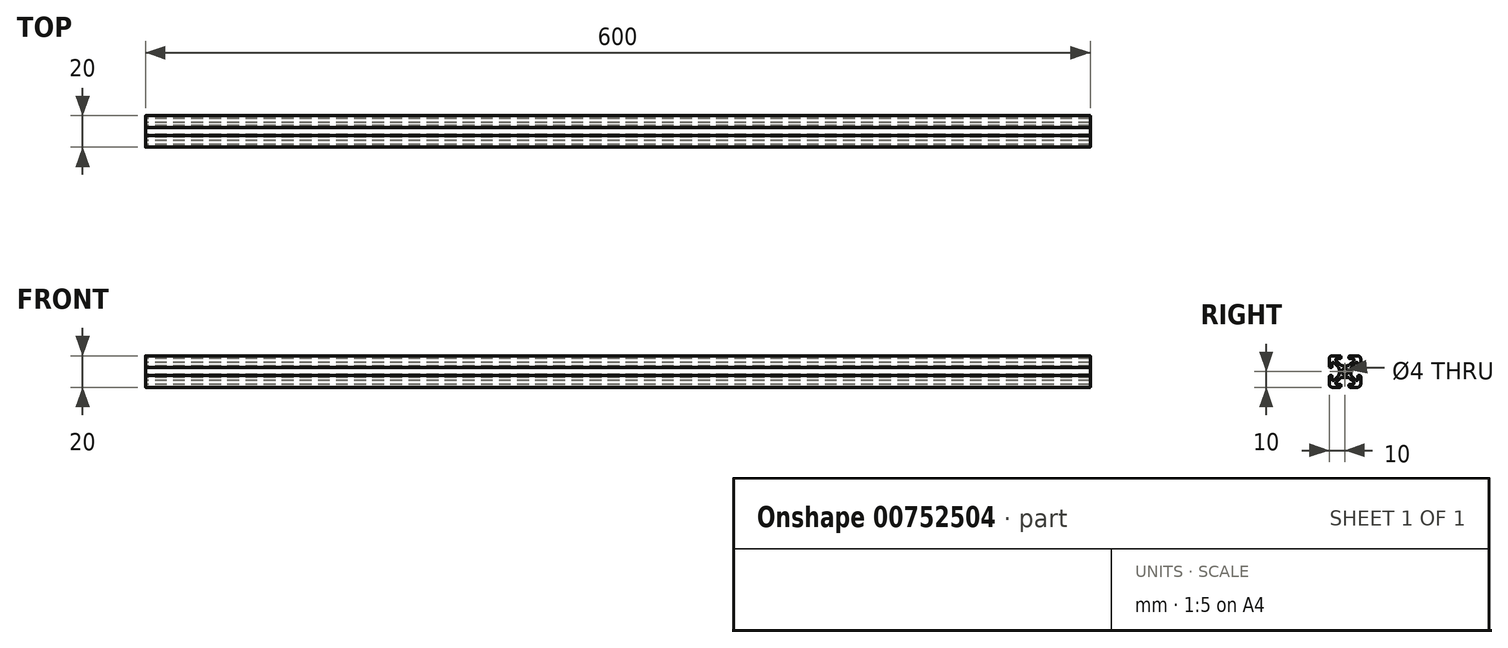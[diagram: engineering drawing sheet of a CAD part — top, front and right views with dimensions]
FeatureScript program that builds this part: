
annotation { "Feature Type Name" : "Feature", "Feature Type Description" : "" }
export const myFeature = defineFeature(function(context is Context, id is Id, definition is map)
    precondition{}
    {
        {
            var Q0;
            Q0=qCreatedBy(makeId("Right.planeOp"),FACE);
            var sketch = newSketch(context, id + "F0", { "sketchPlane" : qUnion([Q0])});
            skLineSegment(sketch, "E0.bottom", {"start": v(-8, 10) * mm, "end": v(-3.3, 10) * mm});
            skLineSegment(sketch, "E0.top", {"start": v(-8, -10) * mm, "end": v(-3.3, -10) * mm});
            skLineSegment(sketch, "E0.right", {"start": v(10, 8) * mm, "end": v(10, 3.3) * mm});
            skLineSegment(sketch, "E1", {"start": v(0, 31.7) * mm, "end": v(0, -24.01) * mm, "construction": true});
            skLineSegment(sketch, "E2", {"start": v(-29.71, 0) * mm, "end": v(21.95, 0) * mm, "construction": true});
            skLineSegment(sketch, "E3", {"start": v(-2.5, 9.2) * mm, "end": v(-2.5, 8.5) * mm});
            skLineSegment(sketch, "E4", {"start": v(-2.8, 8.2) * mm, "end": v(-4.92, 8.2) * mm});
            skLineSegment(sketch, "E5", {"start": v(-5.5, 6.78) * mm, "end": v(-3.25, 4.53) * mm});
            skLineSegment(sketch, "E6", {"start": v(-1.13, 3.65) * mm, "end": v(1.14, 3.65) * mm});
            skLineSegment(sketch, "E7", {"start": v(3.25, 4.53) * mm, "end": v(5.5, 6.78) * mm});
            skLineSegment(sketch, "E8", {"start": v(4.92, 8.2) * mm, "end": v(2.8, 8.2) * mm});
            skLineSegment(sketch, "E9", {"start": v(2.5, 8.5) * mm, "end": v(2.5, 9.2) * mm});
            skLineSegment(sketch, "E10.trimOffspring", {"start": v(3.3, 10) * mm, "end": v(8, 10) * mm});
            skArc(sketch, "E11.filletArc", {"start": v(-8, 10) * mm, "mid": v(-9.41, 9.41) * mm, "end": v(-10, 8) * mm});
            skArc(sketch, "E12.filletArc", {"start": v(-10, -8) * mm, "mid": v(-9.41, -9.41) * mm, "end": v(-8, -10) * mm});
            skArc(sketch, "E13.filletArc", {"start": v(8, -10) * mm, "mid": v(9.41, -9.41) * mm, "end": v(10, -8) * mm});
            skArc(sketch, "E14.filletArc", {"start": v(10, 8) * mm, "mid": v(9.41, 9.41) * mm, "end": v(8, 10) * mm});
            skPoint(sketch, "E15.visualSharp", {"position": v(-9.03, 10.3) * mm});
            skArc(sketch, "E15.filletArc", {"start": v(-4.92, 8.2) * mm, "mid": v(-5.69, 7.69) * mm, "end": v(-5.5, 6.78) * mm});
            skPoint(sketch, "E16.visualSharp", {"position": v(-2.37, 3.65) * mm});
            skArc(sketch, "E16.filletArc", {"start": v(-3.25, 4.53) * mm, "mid": v(-2.28, 3.88) * mm, "end": v(-1.13, 3.65) * mm});
            skPoint(sketch, "E17.visualSharp", {"position": v(2.37, 3.65) * mm});
            skArc(sketch, "E17.filletArc", {"start": v(1.14, 3.65) * mm, "mid": v(2.28, 3.88) * mm, "end": v(3.25, 4.53) * mm});
            skArc(sketch, "E18.filletArc", {"start": v(5.5, 6.78) * mm, "mid": v(5.69, 7.69) * mm, "end": v(4.92, 8.2) * mm});
            skPoint(sketch, "E19.visualSharp", {"position": v(2.5, 8.2) * mm});
            skArc(sketch, "E19.filletArc", {"start": v(2.5, 8.5) * mm, "mid": v(2.59, 8.29) * mm, "end": v(2.8, 8.2) * mm});
            skPoint(sketch, "E20.visualSharp", {"position": v(-2.5, 8.2) * mm});
            skArc(sketch, "E20.filletArc", {"start": v(-2.8, 8.2) * mm, "mid": v(-2.59, 8.29) * mm, "end": v(-2.5, 8.5) * mm});
            skPoint(sketch, "E21.1.5", {"position": v(-3.65, 2.37) * mm});
            skPoint(sketch, "E21.1.13", {"position": v(-10.3, 9.03) * mm});
            skPoint(sketch, "E21.center", {"position": v(0, 0) * mm});
            skLineSegment(sketch, "E22.trimOffspring", {"start": v(-10, -3.3) * mm, "end": v(-10, -8) * mm});
            skLineSegment(sketch, "E23.trimOffspring", {"start": v(10, -3.3) * mm, "end": v(10, -8) * mm});
            skLineSegment(sketch, "E24.trimOffspring", {"start": v(3.3, -10) * mm, "end": v(8, -10) * mm});
            skLineSegment(sketch, "E25", {"start": v(-10, 8) * mm, "end": v(-10, 3.3) * mm});
            skCircle(sketch, "E26", {"center": v(0, 0) * mm, "radius": 2 * mm});
            skPoint(sketch, "E27.visualSharp", {"position": v(-2.5, 10) * mm});
            skArc(sketch, "E27.filletArc", {"start": v(-2.5, 9.2) * mm, "mid": v(-2.73, 9.77) * mm, "end": v(-3.3, 10) * mm});
            skPoint(sketch, "E28.visualSharp", {"position": v(2.5, 10) * mm});
            skArc(sketch, "E28.filletArc", {"start": v(3.3, 10) * mm, "mid": v(2.73, 9.77) * mm, "end": v(2.5, 9.2) * mm});
            skPoint(sketch, "E29.1.1", {"position": v(-10, -2.5) * mm});
            skLineSegment(sketch, "E29.1.2", {"start": v(-3.65, -1.13) * mm, "end": v(-3.65, 1.14) * mm});
            skArc(sketch, "E29.1.3", {"start": v(-4.53, -3.25) * mm, "mid": v(-3.88, -2.28) * mm, "end": v(-3.65, -1.13) * mm});
            skPoint(sketch, "E29.1.4", {"position": v(-8.2, -2.5) * mm});
            skArc(sketch, "E29.1.5", {"start": v(-8.2, -4.92) * mm, "mid": v(-7.69, -5.69) * mm, "end": v(-6.78, -5.5) * mm});
            skLineSegment(sketch, "E29.1.6", {"start": v(-8.2, -2.8) * mm, "end": v(-8.2, -4.92) * mm});
            skLineSegment(sketch, "E29.1.7", {"start": v(-8.2, 4.92) * mm, "end": v(-8.2, 2.8) * mm});
            skArc(sketch, "E29.1.8", {"start": v(-3.65, 1.14) * mm, "mid": v(-3.88, 2.28) * mm, "end": v(-4.53, 3.25) * mm});
            skArc(sketch, "E29.1.9", {"start": v(-6.78, 5.5) * mm, "mid": v(-7.69, 5.69) * mm, "end": v(-8.2, 4.92) * mm});
            skPoint(sketch, "E29.1.10", {"position": v(-3.65, -2.37) * mm});
            skPoint(sketch, "E29.1.11", {"position": v(-10, 2.5) * mm});
            skPoint(sketch, "E29.1.12", {"position": v(-8.2, 2.5) * mm});
            skLineSegment(sketch, "E29.1.13", {"start": v(-6.78, -5.5) * mm, "end": v(-4.53, -3.25) * mm});
            skLineSegment(sketch, "E29.1.14", {"start": v(-4.53, 3.25) * mm, "end": v(-6.78, 5.5) * mm});
            skArc(sketch, "E29.1.15", {"start": v(-10, 3.3) * mm, "mid": v(-9.77, 2.73) * mm, "end": v(-9.2, 2.5) * mm});
            skArc(sketch, "E29.1.16", {"start": v(-9.2, -2.5) * mm, "mid": v(-9.77, -2.73) * mm, "end": v(-10, -3.3) * mm});
            skLineSegment(sketch, "E29.1.17", {"start": v(-8.5, 2.5) * mm, "end": v(-9.2, 2.5) * mm});
            skLineSegment(sketch, "E29.1.18", {"start": v(-9.2, -2.5) * mm, "end": v(-8.5, -2.5) * mm});
            skArc(sketch, "E29.1.19", {"start": v(-8.2, -2.8) * mm, "mid": v(-8.29, -2.59) * mm, "end": v(-8.5, -2.5) * mm});
            skArc(sketch, "E29.1.20", {"start": v(-8.5, 2.5) * mm, "mid": v(-8.29, 2.59) * mm, "end": v(-8.2, 2.8) * mm});
            skPoint(sketch, "E29.2.0", {"position": v(-2.37, -3.65) * mm});
            skPoint(sketch, "E29.2.1", {"position": v(2.5, -10) * mm});
            skLineSegment(sketch, "E29.2.2", {"start": v(1.13, -3.65) * mm, "end": v(-1.14, -3.65) * mm});
            skArc(sketch, "E29.2.3", {"start": v(3.25, -4.53) * mm, "mid": v(2.28, -3.88) * mm, "end": v(1.13, -3.65) * mm});
            skPoint(sketch, "E29.2.4", {"position": v(2.5, -8.2) * mm});
            skArc(sketch, "E29.2.5", {"start": v(4.92, -8.2) * mm, "mid": v(5.69, -7.69) * mm, "end": v(5.5, -6.78) * mm});
            skLineSegment(sketch, "E29.2.6", {"start": v(2.8, -8.2) * mm, "end": v(4.92, -8.2) * mm});
            skLineSegment(sketch, "E29.2.7", {"start": v(-4.92, -8.2) * mm, "end": v(-2.8, -8.2) * mm});
            skArc(sketch, "E29.2.8", {"start": v(-1.14, -3.65) * mm, "mid": v(-2.28, -3.88) * mm, "end": v(-3.25, -4.53) * mm});
            skArc(sketch, "E29.2.9", {"start": v(-5.5, -6.78) * mm, "mid": v(-5.69, -7.69) * mm, "end": v(-4.92, -8.2) * mm});
            skPoint(sketch, "E29.2.10", {"position": v(2.37, -3.65) * mm});
            skPoint(sketch, "E29.2.11", {"position": v(-2.5, -10) * mm});
            skPoint(sketch, "E29.2.12", {"position": v(-2.5, -8.2) * mm});
            skLineSegment(sketch, "E29.2.13", {"start": v(5.5, -6.78) * mm, "end": v(3.25, -4.53) * mm});
            skLineSegment(sketch, "E29.2.14", {"start": v(-3.25, -4.53) * mm, "end": v(-5.5, -6.78) * mm});
            skArc(sketch, "E29.2.15", {"start": v(-3.3, -10) * mm, "mid": v(-2.73, -9.77) * mm, "end": v(-2.5, -9.2) * mm});
            skArc(sketch, "E29.2.16", {"start": v(2.5, -9.2) * mm, "mid": v(2.73, -9.77) * mm, "end": v(3.3, -10) * mm});
            skLineSegment(sketch, "E29.2.17", {"start": v(-2.5, -8.5) * mm, "end": v(-2.5, -9.2) * mm});
            skLineSegment(sketch, "E29.2.18", {"start": v(2.5, -9.2) * mm, "end": v(2.5, -8.5) * mm});
            skArc(sketch, "E29.2.19", {"start": v(2.8, -8.2) * mm, "mid": v(2.59, -8.29) * mm, "end": v(2.5, -8.5) * mm});
            skArc(sketch, "E29.2.20", {"start": v(-2.5, -8.5) * mm, "mid": v(-2.59, -8.29) * mm, "end": v(-2.8, -8.2) * mm});
            skPoint(sketch, "E29.3.0", {"position": v(3.65, -2.37) * mm});
            skPoint(sketch, "E29.3.1", {"position": v(10, 2.5) * mm});
            skLineSegment(sketch, "E29.3.2", {"start": v(3.65, 1.13) * mm, "end": v(3.65, -1.14) * mm});
            skArc(sketch, "E29.3.3", {"start": v(4.53, 3.25) * mm, "mid": v(3.88, 2.28) * mm, "end": v(3.65, 1.13) * mm});
            skPoint(sketch, "E29.3.4", {"position": v(8.2, 2.5) * mm});
            skArc(sketch, "E29.3.5", {"start": v(8.2, 4.92) * mm, "mid": v(7.69, 5.69) * mm, "end": v(6.78, 5.5) * mm});
            skLineSegment(sketch, "E29.3.6", {"start": v(8.2, 2.8) * mm, "end": v(8.2, 4.92) * mm});
            skLineSegment(sketch, "E29.3.7", {"start": v(8.2, -4.92) * mm, "end": v(8.2, -2.8) * mm});
            skArc(sketch, "E29.3.8", {"start": v(3.65, -1.14) * mm, "mid": v(3.88, -2.28) * mm, "end": v(4.53, -3.25) * mm});
            skArc(sketch, "E29.3.9", {"start": v(6.78, -5.5) * mm, "mid": v(7.69, -5.69) * mm, "end": v(8.2, -4.92) * mm});
            skPoint(sketch, "E29.3.10", {"position": v(3.65, 2.37) * mm});
            skPoint(sketch, "E29.3.11", {"position": v(10, -2.5) * mm});
            skPoint(sketch, "E29.3.12", {"position": v(8.2, -2.5) * mm});
            skLineSegment(sketch, "E29.3.13", {"start": v(6.78, 5.5) * mm, "end": v(4.53, 3.25) * mm});
            skLineSegment(sketch, "E29.3.14", {"start": v(4.53, -3.25) * mm, "end": v(6.78, -5.5) * mm});
            skArc(sketch, "E29.3.15", {"start": v(10, -3.3) * mm, "mid": v(9.77, -2.73) * mm, "end": v(9.2, -2.5) * mm});
            skArc(sketch, "E29.3.16", {"start": v(9.2, 2.5) * mm, "mid": v(9.77, 2.73) * mm, "end": v(10, 3.3) * mm});
            skLineSegment(sketch, "E29.3.17", {"start": v(8.5, -2.5) * mm, "end": v(9.2, -2.5) * mm});
            skLineSegment(sketch, "E29.3.18", {"start": v(9.2, 2.5) * mm, "end": v(8.5, 2.5) * mm});
            skArc(sketch, "E29.3.19", {"start": v(8.2, 2.8) * mm, "mid": v(8.29, 2.59) * mm, "end": v(8.5, 2.5) * mm});
            skArc(sketch, "E29.3.20", {"start": v(8.5, -2.5) * mm, "mid": v(8.29, -2.59) * mm, "end": v(8.2, -2.8) * mm});
            skSolve(sketch);
        }
        {
            var Q0;
            Q0=qSketchRegion(id+"F0",true);
            extrude(context, id + "F1", {"entities" : qUnion([Q0]), "depth" : 600 * mm, "offsetDistance" : 25 * mm});
        }
    });
